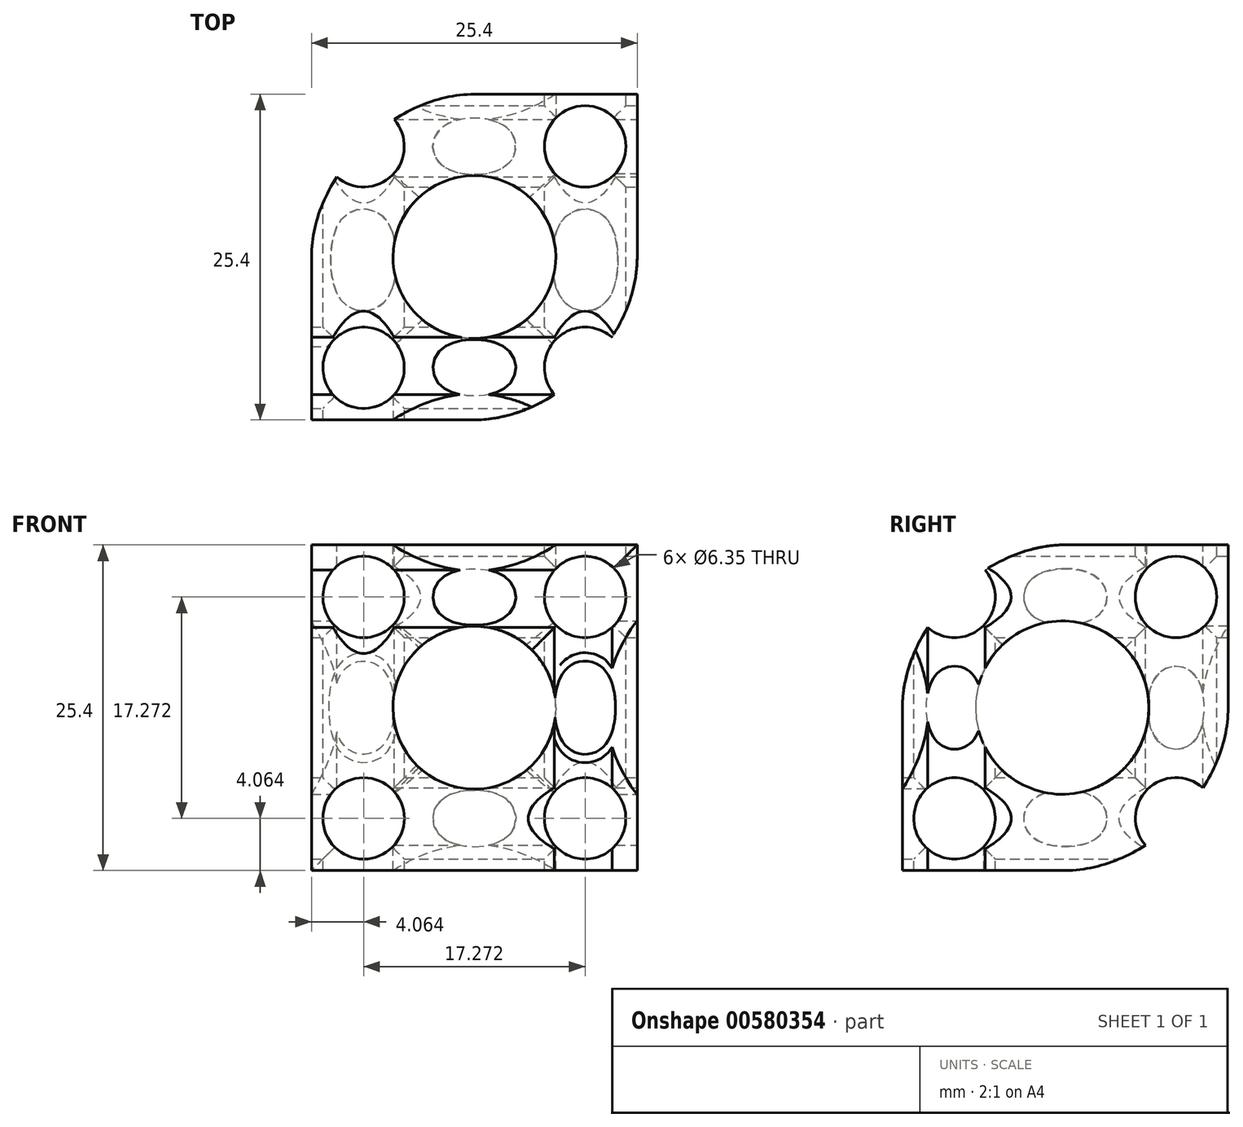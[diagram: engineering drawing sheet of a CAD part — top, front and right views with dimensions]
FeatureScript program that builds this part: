
annotation { "Feature Type Name" : "Feature", "Feature Type Description" : "" }
export const myFeature = defineFeature(function(context is Context, id is Id, definition is map)
    precondition{}
    {
        {
            var Q0;
            Q0=qCreatedBy(makeId("Front.planeOp"),FACE);
            var sketch = newSketch(context, id + "F0", { "sketchPlane" : qUnion([Q0])});
            skLineSegment(sketch, "E0.bottom", {"start": v(-12.7, 12.7) * mm, "end": v(12.7, 12.7) * mm});
            skLineSegment(sketch, "E0.top", {"start": v(-12.7, -12.7) * mm, "end": v(12.7, -12.7) * mm});
            skLineSegment(sketch, "E0.left", {"start": v(-12.7, 12.7) * mm, "end": v(-12.7, -12.7) * mm});
            skLineSegment(sketch, "E0.right", {"start": v(12.7, 12.7) * mm, "end": v(12.7, -12.7) * mm});
            skPoint(sketch, "E0.middle", {"position": v(0, 0) * mm});
            skSolve(sketch);
        }
        {
            var Q0;
            Q0=makeQuery(id+"F0.imprint","IMPRINT",FACE,{"disambiguationData":[TD([[makeQuery(id+"F0.imprint","IMPRINT",EDGE,{"derivedFrom":sQuery(id+"F0.wireOp",EDGE,"E0.bottom")}),-1.0]])]});
            extrude(context, id + "F1", {"entities" : qUnion([Q0]), "depth" : 25.4 * mm, "offsetDistance" : 25.4 * mm});
        }
        {
            var Q0;
            Q0=makeQuery(id+"F1.opExtrude","SWEPT_FACE",FACE,{"disambiguationData":[OSD([sQuery(id+"F0.wireOp",EDGE,"E0.bottom")])]});
            var sketch = newSketch(context, id + "F2", { "sketchPlane" : qUnion([Q0])});
            skCircle(sketch, "E1", {"center": v(0, -12.7) * mm, "radius": 6.35 * mm});
            skSolve(sketch);
        }
        {
            var Q0;
            Q0=makeQuery(id+"F2.imprint","IMPRINT",FACE,{"disambiguationData":[TD([[makeQuery(id+"F2.imprint","IMPRINT",EDGE,{"derivedFrom":sQuery(id+"F2.wireOp",EDGE,"E1")}),1.0]])]});
            extrude(context, id + "F3", {"entities" : qUnion([Q0]), "operationType" : NewBodyOperationType.REMOVE, "oppositeDirection" : true, "depth" : 25.4 * mm, "offsetDistance" : 25.4 * mm});
        }
        {
            var Q0;
            Q0=makeQuery(id+"F1.opExtrude","CAP_FACE",FACE,{"disambiguationData":[OSD([sQuery(id+"F0.wireOp",EDGE,"E0.bottom"),sQuery(id+"F0.wireOp",EDGE,"E0.top"),sQuery(id+"F0.wireOp",EDGE,"E0.left"),sQuery(id+"F0.wireOp",EDGE,"E0.right")])],"isStart":false});
            var sketch = newSketch(context, id + "F4", { "sketchPlane" : qUnion([Q0])});
            skCircle(sketch, "E2", {"center": v(0, 0) * mm, "radius": 6.35 * mm});
            skSolve(sketch);
        }
        {
            var Q0;
            Q0=makeQuery(id+"F4.imprint","IMPRINT",FACE,{"disambiguationData":[TD([[makeQuery(id+"F4.imprint","IMPRINT",EDGE,{"derivedFrom":sQuery(id+"F4.wireOp",EDGE,"E2")}),1.0]])]});
            extrude(context, id + "F5", {"entities" : qUnion([Q0]), "operationType" : NewBodyOperationType.REMOVE, "oppositeDirection" : true, "depth" : 25.4 * mm, "offsetDistance" : 25.4 * mm});
        }
        {
            var Q0;
            Q0=makeQuery(id+"F1.opExtrude","SWEPT_FACE",FACE,{"disambiguationData":[OSD([sQuery(id+"F0.wireOp",EDGE,"E0.right")])]});
            var sketch = newSketch(context, id + "F6", { "sketchPlane" : qUnion([Q0])});
            skCircle(sketch, "E3", {"center": v(-12.93, 0) * mm, "radius": 6.76 * mm});
            skSolve(sketch);
        }
        {
            var Q0;
            Q0=makeQuery(id+"F6.imprint","IMPRINT",FACE,{"disambiguationData":[TD([[makeQuery(id+"F6.imprint","IMPRINT",EDGE,{"derivedFrom":sQuery(id+"F6.wireOp",EDGE,"E3")}),1.0]])]});
            extrude(context, id + "F7", {"entities" : qUnion([Q0]), "operationType" : NewBodyOperationType.REMOVE, "oppositeDirection" : true, "depth" : 25.4 * mm, "offsetDistance" : 25.4 * mm});
        }
        {
            var Q0;
            Q0=makeQuery(id+"F1.opExtrude","SWEPT_FACE",FACE,{"disambiguationData":[OSD([sQuery(id+"F0.wireOp",EDGE,"E0.right")])]});
            var sketch = newSketch(context, id + "F8", { "sketchPlane" : qUnion([Q0])});
            skCircle(sketch, "E4", {"center": v(-4.06, 8.64) * mm, "radius": 3.17 * mm});
            skSolve(sketch);
        }
        {
            var Q0;
            Q0=makeQuery(id+"F8.imprint","IMPRINT",FACE,{"disambiguationData":[TD([[makeQuery(id+"F8.imprint","IMPRINT",EDGE,{"derivedFrom":sQuery(id+"F8.wireOp",EDGE,"E4")}),1.0]])]});
            extrude(context, id + "F9", {"entities" : qUnion([Q0]), "operationType" : NewBodyOperationType.REMOVE, "oppositeDirection" : true, "depth" : 25.4 * mm, "offsetDistance" : 25.4 * mm});
        }
        {
            var Q0;
            Q0=makeQuery(id+"F1.opExtrude","SWEPT_FACE",FACE,{"disambiguationData":[OSD([sQuery(id+"F0.wireOp",EDGE,"E0.right")])]});
            var sketch = newSketch(context, id + "F10", { "sketchPlane" : qUnion([Q0])});
            skCircle(sketch, "E5", {"center": v(-21.34, 8.64) * mm, "radius": 3.18 * mm});
            skSolve(sketch);
        }
        {
            var Q0;
            Q0=makeQuery(id+"F10.imprint","IMPRINT",FACE,{"disambiguationData":[TD([[makeQuery(id+"F10.imprint","IMPRINT",EDGE,{"derivedFrom":sQuery(id+"F10.wireOp",EDGE,"E5")}),1.0]])]});
            extrude(context, id + "F11", {"entities" : qUnion([Q0]), "operationType" : NewBodyOperationType.REMOVE, "oppositeDirection" : true, "depth" : 25.4 * mm, "offsetDistance" : 25.4 * mm});
        }
        {
            var Q0;
            Q0=makeQuery(id+"F1.opExtrude","SWEPT_FACE",FACE,{"disambiguationData":[OSD([sQuery(id+"F0.wireOp",EDGE,"E0.right")])]});
            var sketch = newSketch(context, id + "F12", { "sketchPlane" : qUnion([Q0])});
            skCircle(sketch, "E6", {"center": v(-21.34, -8.64) * mm, "radius": 3.18 * mm});
            skSolve(sketch);
        }
        {
            var Q0;
            Q0=makeQuery(id+"F12.imprint","IMPRINT",FACE,{"disambiguationData":[TD([[makeQuery(id+"F12.imprint","IMPRINT",EDGE,{"derivedFrom":sQuery(id+"F12.wireOp",EDGE,"E6")}),1.0]])]});
            extrude(context, id + "F13", {"entities" : qUnion([Q0]), "operationType" : NewBodyOperationType.REMOVE, "oppositeDirection" : true, "depth" : 25.4 * mm, "offsetDistance" : 25.4 * mm});
        }
        {
            var Q0;
            Q0=makeQuery(id+"F1.opExtrude","SWEPT_FACE",FACE,{"disambiguationData":[OSD([sQuery(id+"F0.wireOp",EDGE,"E0.right")])]});
            var sketch = newSketch(context, id + "F14", { "sketchPlane" : qUnion([Q0])});
            skCircle(sketch, "E7", {"center": v(-4.06, -8.64) * mm, "radius": 3.18 * mm});
            skSolve(sketch);
        }
        {
            var Q0;
            Q0=makeQuery(id+"F14.imprint","IMPRINT",FACE,{"disambiguationData":[TD([[makeQuery(id+"F14.imprint","IMPRINT",EDGE,{"derivedFrom":sQuery(id+"F14.wireOp",EDGE,"E7")}),1.0]])]});
            extrude(context, id + "F15", {"entities" : qUnion([Q0]), "operationType" : NewBodyOperationType.REMOVE, "oppositeDirection" : true, "depth" : 25.4 * mm, "offsetDistance" : 25.4 * mm});
        }
        {
            var Q0;
            Q0=makeQuery(id+"F1.opExtrude","CAP_FACE",FACE,{"disambiguationData":[OSD([sQuery(id+"F0.wireOp",EDGE,"E0.bottom"),sQuery(id+"F0.wireOp",EDGE,"E0.top"),sQuery(id+"F0.wireOp",EDGE,"E0.left"),sQuery(id+"F0.wireOp",EDGE,"E0.right")])],"isStart":true});
            var sketch = newSketch(context, id + "F16", { "sketchPlane" : qUnion([Q0])});
            skCircle(sketch, "E8", {"center": v(-8.64, 8.64) * mm, "radius": 3.18 * mm});
            skSolve(sketch);
        }
        {
            var Q0;
            Q0=makeQuery(id+"F16.imprint","IMPRINT",FACE,{"disambiguationData":[TD([[makeQuery(id+"F16.imprint","IMPRINT",EDGE,{"derivedFrom":sQuery(id+"F16.wireOp",EDGE,"E8")}),1.0]])]});
            extrude(context, id + "F17", {"entities" : qUnion([Q0]), "operationType" : NewBodyOperationType.REMOVE, "oppositeDirection" : true, "depth" : 25.4 * mm, "offsetDistance" : 25.4 * mm});
        }
        {
            var Q0;
            Q0=makeQuery(id+"F1.opExtrude","CAP_FACE",FACE,{"disambiguationData":[OSD([sQuery(id+"F0.wireOp",EDGE,"E0.bottom"),sQuery(id+"F0.wireOp",EDGE,"E0.top"),sQuery(id+"F0.wireOp",EDGE,"E0.left"),sQuery(id+"F0.wireOp",EDGE,"E0.right")])],"isStart":true});
            var sketch = newSketch(context, id + "F18", { "sketchPlane" : qUnion([Q0])});
            skCircle(sketch, "E9", {"center": v(8.64, 8.64) * mm, "radius": 3.18 * mm});
            skSolve(sketch);
        }
        {
            var Q0;
            Q0=makeQuery(id+"F18.imprint","IMPRINT",FACE,{"disambiguationData":[TD([[makeQuery(id+"F18.imprint","IMPRINT",EDGE,{"derivedFrom":sQuery(id+"F18.wireOp",EDGE,"E9")}),1.0]])]});
            extrude(context, id + "F19", {"entities" : qUnion([Q0]), "operationType" : NewBodyOperationType.REMOVE, "oppositeDirection" : true, "depth" : 25.4 * mm, "offsetDistance" : 25.4 * mm});
        }
        {
            var Q0;
            Q0=makeQuery(id+"F1.opExtrude","CAP_FACE",FACE,{"disambiguationData":[OSD([sQuery(id+"F0.wireOp",EDGE,"E0.bottom"),sQuery(id+"F0.wireOp",EDGE,"E0.top"),sQuery(id+"F0.wireOp",EDGE,"E0.left"),sQuery(id+"F0.wireOp",EDGE,"E0.right")])],"isStart":true});
            var sketch = newSketch(context, id + "F20", { "sketchPlane" : qUnion([Q0])});
            skCircle(sketch, "E10", {"center": v(-8.64, -8.64) * mm, "radius": 3.18 * mm});
            skSolve(sketch);
        }
        {
            var Q0;
            Q0=makeQuery(id+"F20.imprint","IMPRINT",FACE,{"disambiguationData":[TD([[makeQuery(id+"F20.imprint","IMPRINT",EDGE,{"derivedFrom":sQuery(id+"F20.wireOp",EDGE,"E10")}),1.0]])]});
            extrude(context, id + "F21", {"entities" : qUnion([Q0]), "operationType" : NewBodyOperationType.REMOVE, "oppositeDirection" : true, "depth" : 25.4 * mm, "offsetDistance" : 25.4 * mm});
        }
        {
            var Q0;
            Q0=makeQuery(id+"F1.opExtrude","CAP_FACE",FACE,{"disambiguationData":[OSD([sQuery(id+"F0.wireOp",EDGE,"E0.bottom"),sQuery(id+"F0.wireOp",EDGE,"E0.top"),sQuery(id+"F0.wireOp",EDGE,"E0.left"),sQuery(id+"F0.wireOp",EDGE,"E0.right")])],"isStart":true});
            var sketch = newSketch(context, id + "F22", { "sketchPlane" : qUnion([Q0])});
            skCircle(sketch, "E11", {"center": v(8.64, -8.64) * mm, "radius": 3.18 * mm});
            skSolve(sketch);
        }
        {
            var Q0;
            Q0=makeQuery(id+"F22.imprint","IMPRINT",FACE,{"disambiguationData":[TD([[makeQuery(id+"F22.imprint","IMPRINT",EDGE,{"derivedFrom":sQuery(id+"F22.wireOp",EDGE,"E11")}),1.0]])]});
            extrude(context, id + "F23", {"entities" : qUnion([Q0]), "operationType" : NewBodyOperationType.REMOVE, "oppositeDirection" : true, "depth" : 25.4 * mm, "offsetDistance" : 25.4 * mm});
        }
        {
            var Q0;
            Q0=makeQuery(id+"F1.opExtrude","SWEPT_FACE",FACE,{"disambiguationData":[OSD([sQuery(id+"F0.wireOp",EDGE,"E0.bottom")])]});
            var sketch = newSketch(context, id + "F24", { "sketchPlane" : qUnion([Q0])});
            skCircle(sketch, "E12", {"center": v(-8.64, -4.06) * mm, "radius": 3.18 * mm});
            skSolve(sketch);
        }
        {
            var Q0;
            Q0=makeQuery(id+"F24.imprint","IMPRINT",FACE,{"disambiguationData":[TD([[makeQuery(id+"F24.imprint","IMPRINT",EDGE,{"derivedFrom":sQuery(id+"F24.wireOp",EDGE,"E12")}),1.0]])]});
            extrude(context, id + "F25", {"entities" : qUnion([Q0]), "operationType" : NewBodyOperationType.REMOVE, "oppositeDirection" : true, "depth" : 25.4 * mm, "offsetDistance" : 25.4 * mm});
        }
        {
            var Q0;
            Q0=makeQuery(id+"F1.opExtrude","SWEPT_FACE",FACE,{"disambiguationData":[OSD([sQuery(id+"F0.wireOp",EDGE,"E0.bottom")])]});
            var sketch = newSketch(context, id + "F26", { "sketchPlane" : qUnion([Q0])});
            skCircle(sketch, "E13", {"center": v(8.64, -4.06) * mm, "radius": 3.18 * mm});
            skSolve(sketch);
        }
        {
            var Q0;
            Q0=makeQuery(id+"F26.imprint","IMPRINT",FACE,{"disambiguationData":[TD([[makeQuery(id+"F26.imprint","IMPRINT",EDGE,{"derivedFrom":sQuery(id+"F26.wireOp",EDGE,"E13")}),1.0]])]});
            extrude(context, id + "F27", {"entities" : qUnion([Q0]), "operationType" : NewBodyOperationType.REMOVE, "oppositeDirection" : true, "depth" : 25.4 * mm, "offsetDistance" : 25.4 * mm});
        }
        {
            var Q0;
            Q0=makeQuery(id+"F1.opExtrude","SWEPT_FACE",FACE,{"disambiguationData":[OSD([sQuery(id+"F0.wireOp",EDGE,"E0.bottom")])]});
            var sketch = newSketch(context, id + "F28", { "sketchPlane" : qUnion([Q0])});
            skCircle(sketch, "E14", {"center": v(-8.64, -21.34) * mm, "radius": 3.18 * mm});
            skSolve(sketch);
        }
        {
            var Q0;
            Q0=makeQuery(id+"F28.imprint","IMPRINT",FACE,{"disambiguationData":[TD([[makeQuery(id+"F28.imprint","IMPRINT",EDGE,{"derivedFrom":sQuery(id+"F28.wireOp",EDGE,"E14")}),1.0]])]});
            extrude(context, id + "F29", {"entities" : qUnion([Q0]), "operationType" : NewBodyOperationType.REMOVE, "oppositeDirection" : true, "depth" : 25.4 * mm, "offsetDistance" : 25.4 * mm});
        }
        {
            var Q0;
            Q0=makeQuery(id+"F1.opExtrude","SWEPT_FACE",FACE,{"disambiguationData":[OSD([sQuery(id+"F0.wireOp",EDGE,"E0.bottom")])]});
            var sketch = newSketch(context, id + "F30", { "sketchPlane" : qUnion([Q0])});
            skCircle(sketch, "E15", {"center": v(8.64, -21.34) * mm, "radius": 3.18 * mm});
            skSolve(sketch);
        }
        {
            var Q0;
            Q0=makeQuery(id+"F30.imprint","IMPRINT",FACE,{"disambiguationData":[TD([[makeQuery(id+"F30.imprint","IMPRINT",EDGE,{"derivedFrom":sQuery(id+"F30.wireOp",EDGE,"E15")}),1.0]])]});
            extrude(context, id + "F31", {"entities" : qUnion([Q0]), "operationType" : NewBodyOperationType.REMOVE, "oppositeDirection" : true, "depth" : 25.4 * mm, "offsetDistance" : 25.4 * mm});
        }
        {
            var Q0;
            Q0=makeQuery(id+"F1.opExtrude","SWEPT_FACE",FACE,{"disambiguationData":[OSD([sQuery(id+"F0.wireOp",EDGE,"E0.bottom")])]});
            var sketch = newSketch(context, id + "F32", { "sketchPlane" : qUnion([Q0])});
            skFitSpline(sketch, "E16", {"points": [v(0, 0) * mm, v(12.7, -12.7) * mm, v(0, -25.4) * mm, v(-12.7, -12.7) * mm, v(0, 0) * mm]});
            skSolve(sketch);
        }
        {
            var Q0;
            {var subQ0=sQuery(id+"F0.wireOp",EDGE,"E0.bottom");var subQ1=makeQuery(id+"F1.opExtrude","CAP_EDGE",EDGE,{"disambiguationData":[OSD([subQ0])],"isStart":true});var subQ4=sQuery(id+"F32.wireOp",EDGE,"E16");var subQ5=makeQuery(id+"F32.imprint","INTERSECT",VERTEX,{"derivedFrom":[subQ1,subQ4]});Q0=makeQuery(id+"F32.imprint","IMPRINT",FACE,{"disambiguationData":[TD([[makeQuery(id+"F32.imprint","IMPRINT",EDGE,{"disambiguationData":[TD([[subQ5,1.0]])],"derivedFrom":subQ4}),1.0]])]});}
            extrude(context, id + "F33", {"entities" : qUnion([Q0]), "operationType" : NewBodyOperationType.REMOVE, "oppositeDirection" : true, "depth" : 25.4 * mm, "offsetDistance" : 25.4 * mm});
        }
        {
            var Q0;
            Q0=makeQuery(id+"F1.opExtrude","SWEPT_FACE",FACE,{"disambiguationData":[OSD([sQuery(id+"F0.wireOp",EDGE,"E0.bottom")])]});
            var sketch = newSketch(context, id + "F34", { "sketchPlane" : qUnion([Q0])});
            skFitSpline(sketch, "E17", {"points": [v(0, 0) * mm, v(12.7, -12.7) * mm, v(0, -25.4) * mm, v(-12.7, -12.7) * mm, v(0, 0) * mm]});
            skSolve(sketch);
        }
        {
            var Q0;
            {var subQ0=sQuery(id+"F0.wireOp",EDGE,"E0.bottom");var subQ1=makeQuery(id+"F1.opExtrude","CAP_EDGE",EDGE,{"disambiguationData":[OSD([subQ0])],"isStart":false});var subQ4=sQuery(id+"F34.wireOp",EDGE,"E17");var subQ5=makeQuery(id+"F34.imprint","INTERSECT",VERTEX,{"derivedFrom":[subQ1,subQ4]});Q0=makeQuery(id+"F34.imprint","IMPRINT",FACE,{"disambiguationData":[TD([[makeQuery(id+"F34.imprint","IMPRINT",EDGE,{"disambiguationData":[TD([[subQ5,1.0]])],"derivedFrom":subQ4}),1.0]])]});}
            extrude(context, id + "F35", {"entities" : qUnion([Q0]), "operationType" : NewBodyOperationType.REMOVE, "oppositeDirection" : true, "depth" : 25.4 * mm, "offsetDistance" : 25.4 * mm});
        }
        {
            var Q0;
            Q0=makeQuery(id+"F1.opExtrude","SWEPT_FACE",FACE,{"disambiguationData":[OSD([sQuery(id+"F0.wireOp",EDGE,"E0.right")])]});
            var sketch = newSketch(context, id + "F36", { "sketchPlane" : qUnion([Q0])});
            skPoint(sketch, "E18.3.internal.snap0", {"position": v(-6.17, 0) * mm});
            skFitSpline(sketch, "E18", {"points": [v(-12.7, 12.7) * mm, v(0, 0) * mm, v(-12.7, -12.7) * mm, v(-25.72, 0) * mm, v(-12.7, 12.7) * mm]});
            skSolve(sketch);
        }
        {
            var Q0;
            {var subQ1=sQuery(id+"F0.wireOp",EDGE,"E0.top");var subQ3=sQuery(id+"F0.wireOp",EDGE,"E0.right");var subQ9=makeQuery(id+"F1.opExtrude","SWEPT_EDGE",EDGE,{"disambiguationData":[OSD([subQ1,subQ3])]});Q0=makeQuery(id+"F36.imprint","IMPRINT",FACE,{"disambiguationData":[TD([[makeQuery(id+"F36.imprint","IMPRINT",EDGE,{"derivedFrom":subQ9}),1.0]])]});}
            extrude(context, id + "F37", {"entities" : qUnion([Q0]), "operationType" : NewBodyOperationType.REMOVE, "oppositeDirection" : true, "depth" : 25.4 * mm, "offsetDistance" : 25.4 * mm});
        }
        {
            var Q0;
            Q0=makeQuery(id+"F1.opExtrude","SWEPT_FACE",FACE,{"disambiguationData":[OSD([sQuery(id+"F0.wireOp",EDGE,"E0.left")])]});
            var sketch = newSketch(context, id + "F38", { "sketchPlane" : qUnion([Q0])});
            skFitSpline(sketch, "E19", {"points": [v(12.7, 12.7) * mm, v(25.4, 0) * mm, v(12.7, -12.7) * mm, v(0, 0) * mm, v(12.7, 12.7) * mm]});
            skSolve(sketch);
        }
        {
            var Q0;
            {var subQ0=sQuery(id+"F0.wireOp",EDGE,"E0.left");var subQ1=sQuery(id+"F0.wireOp",EDGE,"E0.bottom");var subQ2=makeQuery(id+"F1.opExtrude","SWEPT_EDGE",EDGE,{"disambiguationData":[OSD([subQ1,subQ0])]});var subQ3=subQ2;Q0=makeQuery(id+"F38.imprint","IMPRINT",FACE,{"disambiguationData":[TD([[makeQuery(id+"F38.imprint","IMPRINT",EDGE,{"derivedFrom":subQ3}),1.0]])]});}
            extrude(context, id + "F39", {"entities" : qUnion([Q0]), "operationType" : NewBodyOperationType.REMOVE, "oppositeDirection" : true, "depth" : 25.4 * mm, "offsetDistance" : 25.4 * mm});
        }
    });
